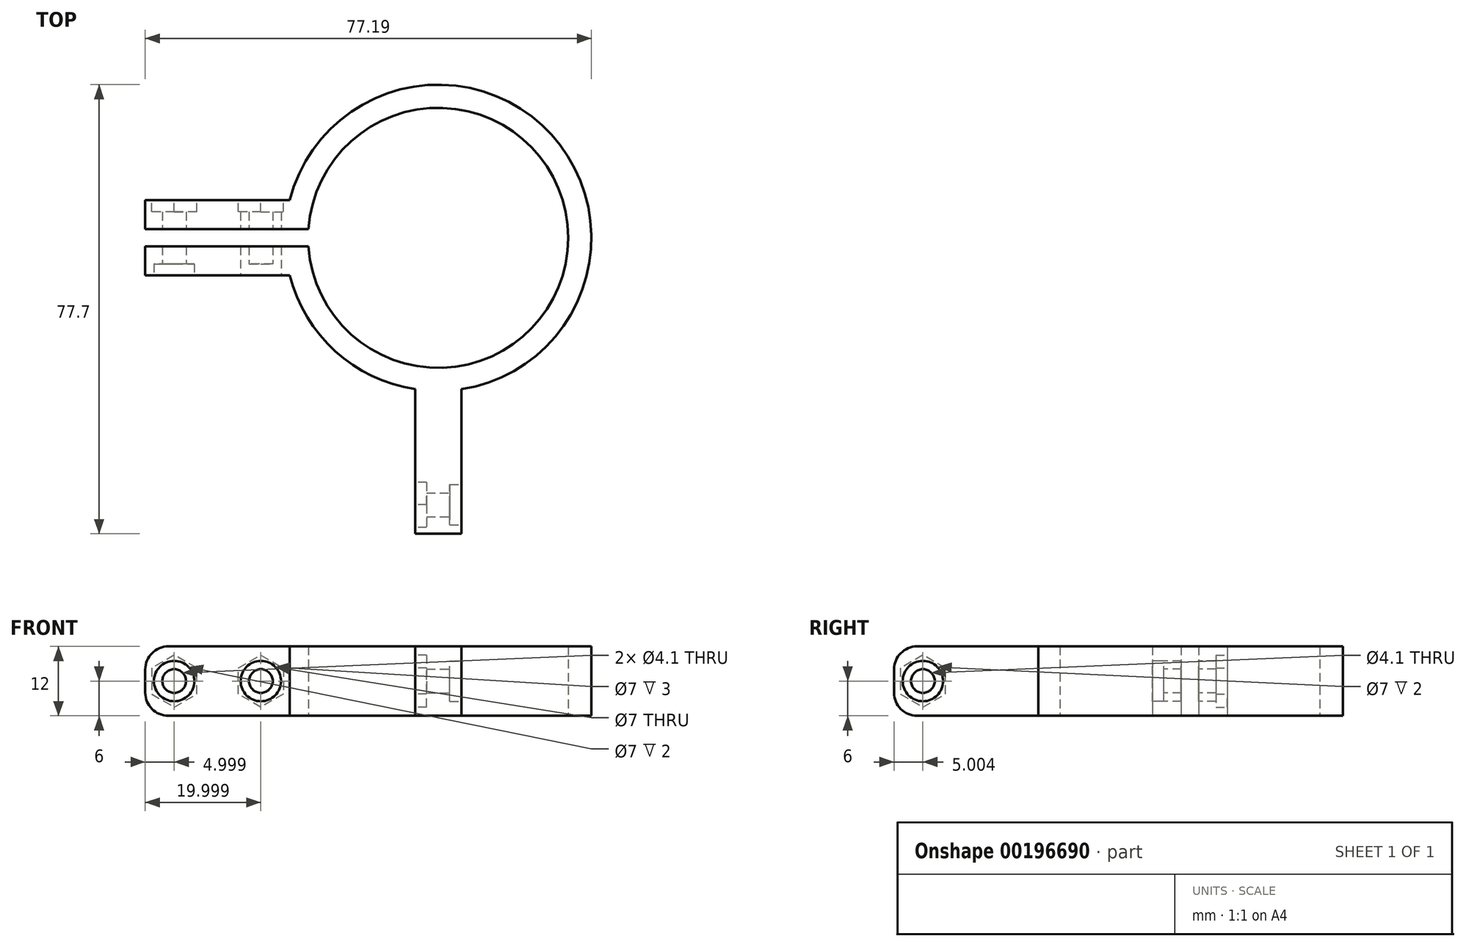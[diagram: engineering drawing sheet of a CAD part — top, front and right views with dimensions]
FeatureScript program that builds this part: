
annotation { "Feature Type Name" : "Feature", "Feature Type Description" : "" }
export const myFeature = defineFeature(function(context is Context, id is Id, definition is map)
    precondition{}
    {
        {
            var Q0;
            Q0=qCreatedBy(makeId("Top.planeOp"),FACE);
            var sketch = newSketch(context, id + "F0", { "sketchPlane" : qUnion([Q0])});
            skArc(sketch, "E0", {"start": v(-22.45, -1.5) * mm, "mid": v(22.5, 0) * mm, "end": v(-22.45, 1.5) * mm});
            skLineSegment(sketch, "E1.top", {"start": v(-25.7, -6.5) * mm, "end": v(-50.7, -6.5) * mm});
            skLineSegment(sketch, "E1.right", {"start": v(-50.7, 6.5) * mm, "end": v(-50.7, 1.5) * mm});
            skLineSegment(sketch, "E2", {"start": v(-22.45, 1.5) * mm, "end": v(-50.7, 1.5) * mm});
            skLineSegment(sketch, "E3", {"start": v(-22.45, -1.5) * mm, "end": v(-50.7, -1.5) * mm});
            skLineSegment(sketch, "E4.trimOffspring", {"start": v(-50.7, -1.5) * mm, "end": v(-50.7, -6.5) * mm});
            skLineSegment(sketch, "E5.trimOffspring", {"start": v(-25.7, 6.5) * mm, "end": v(-50.7, 6.5) * mm});
            skArc(sketch, "E6", {"start": v(-25.7, -6.5) * mm, "mid": v(-17.81, -19.62) * mm, "end": v(-4, -26.2) * mm});
            skLineSegment(sketch, "E7", {"start": v(0, 0) * mm, "end": v(-63.81, 0) * mm, "construction": true});
            skLineSegment(sketch, "E8", {"start": v(0, 0) * mm, "end": v(0, -56.86) * mm, "construction": true});
            skLineSegment(sketch, "E9.top", {"start": v(-4, -51.2) * mm, "end": v(4, -51.2) * mm});
            skLineSegment(sketch, "E9.left", {"start": v(-4, -26.2) * mm, "end": v(-4, -51.2) * mm});
            skLineSegment(sketch, "E9.right", {"start": v(4, -26.2) * mm, "end": v(4, -51.2) * mm});
            skArc(sketch, "E10.trimOffspring", {"start": v(4, -26.2) * mm, "mid": v(19.62, 17.81) * mm, "end": v(-25.7, 6.5) * mm});
            skSolve(sketch);
        }
        {
            var Q0;
            Q0=makeQuery(id+"F0.imprint","IMPRINT",FACE,{"disambiguationData":[TD([[makeQuery(id+"F0.imprint","IMPRINT",EDGE,{"derivedFrom":sQuery(id+"F0.wireOp",EDGE,"E0")}),-1.0]])]});
            extrude(context, id + "F1", {"entities" : qUnion([Q0]), "endBound" : BoundingType.SYMMETRIC, "depth" : 12 * mm});
        }
        {
            var Q0;
            Q0=makeQuery(id+"F1.opExtrude","SWEPT_FACE",FACE,{"disambiguationData":[OSD([sQuery(id+"F0.wireOp",EDGE,"E1.top")])]});
            var sketch = newSketch(context, id + "F2", { "sketchPlane" : qUnion([Q0])});
            skLineSegment(sketch, "E11", {"start": v(0, 0) * mm, "end": v(-145.87, 0) * mm, "construction": true});
            skPoint(sketch, "E12", {"position": v(-45.7, 0) * mm});
            skCircle(sketch, "E13", {"center": v(-45.7, 0) * mm, "radius": 2.05 * mm});
            skCircle(sketch, "E14", {"center": v(-45.7, 0) * mm, "radius": 3.5 * mm});
            skLineSegment(sketch, "E15", {"start": v(-38.2, 6) * mm, "end": v(-38.2, -6) * mm, "construction": true});
            skPoint(sketch, "E16.MirrorP", {"position": v(-30.7, 0) * mm});
            skCircle(sketch, "E17.MirrorC", {"center": v(-30.7, 0) * mm, "radius": 2.05 * mm});
            skCircle(sketch, "E18.MirrorC", {"center": v(-30.7, 0) * mm, "radius": 3.5 * mm});
            skSolve(sketch);
        }
        {
            var Q0;
            Q0=makeQuery(id+"F1.opExtrude","SWEPT_FACE",FACE,{"disambiguationData":[OSD([sQuery(id+"F0.wireOp",EDGE,"E5.trimOffspring")])]});
            var sketch = newSketch(context, id + "F3", { "sketchPlane" : qUnion([Q0])});
            skPoint(sketch, "E19", {"position": v(45.7, 0) * mm});
            skPoint(sketch, "E19.positionSnap0", {"position": v(50.7, 0) * mm});
            skCircle(sketch, "E20.cCircle", {"center": v(45.7, 0) * mm, "radius": 3.9 * mm, "construction": true});
            skLineSegment(sketch, "E20.0", {"start": v(49.59, 2.25) * mm, "end": v(49.59, -2.25) * mm});
            skLineSegment(sketch, "E20.1", {"start": v(49.59, -2.25) * mm, "end": v(45.7, -4.5) * mm});
            skLineSegment(sketch, "E20.2", {"start": v(45.7, -4.5) * mm, "end": v(41.8, -2.25) * mm});
            skLineSegment(sketch, "E20.3", {"start": v(41.8, -2.25) * mm, "end": v(41.8, 2.25) * mm});
            skLineSegment(sketch, "E20.4", {"start": v(41.8, 2.25) * mm, "end": v(45.7, 4.5) * mm});
            skLineSegment(sketch, "E20.5", {"start": v(45.7, 4.5) * mm, "end": v(49.59, 2.25) * mm});
            skPoint(sketch, "E20.0.midPoint", {"position": v(49.59, 0) * mm});
            skLineSegment(sketch, "E21", {"start": v(38.2, 6) * mm, "end": v(38.2, -6) * mm, "construction": true});
            skLineSegment(sketch, "E22.MirrorCS", {"start": v(30.7, 4.5) * mm, "end": v(26.8, 2.25) * mm});
            skLineSegment(sketch, "E23.MirrorCS", {"start": v(26.8, 2.25) * mm, "end": v(26.8, -2.25) * mm});
            skLineSegment(sketch, "E24.MirrorCS", {"start": v(30.7, -4.5) * mm, "end": v(34.59, -2.25) * mm});
            skLineSegment(sketch, "E25.MirrorCS", {"start": v(34.59, -2.25) * mm, "end": v(34.59, 2.25) * mm});
            skCircle(sketch, "E26.MirrorC", {"center": v(30.7, 0) * mm, "radius": 3.9 * mm, "construction": true});
            skPoint(sketch, "E27.MirrorP", {"position": v(26.8, 0) * mm});
            skLineSegment(sketch, "E28.MirrorCS", {"start": v(26.8, -2.25) * mm, "end": v(30.7, -4.5) * mm});
            skLineSegment(sketch, "E29.MirrorCS", {"start": v(34.59, 2.25) * mm, "end": v(30.7, 4.5) * mm});
            skSolve(sketch);
        }
        {
            var Q0;
            Q0=makeQuery(id+"F1.opExtrude","SWEPT_FACE",FACE,{"disambiguationData":[OSD([sQuery(id+"F0.wireOp",EDGE,"E9.right")])]});
            var sketch = newSketch(context, id + "F4", { "sketchPlane" : qUnion([Q0])});
            skLineSegment(sketch, "E30", {"start": v(0, 0) * mm, "end": v(-57.41, 0) * mm, "construction": true});
            skPoint(sketch, "E30.endSnap0", {"position": v(-51.2, 0) * mm});
            skPoint(sketch, "E31", {"position": v(-46.2, 0) * mm});
            skCircle(sketch, "E32", {"center": v(-46.2, 0) * mm, "radius": 2.05 * mm});
            skCircle(sketch, "E33", {"center": v(-46.2, 0) * mm, "radius": 3.5 * mm});
            skSolve(sketch);
        }
        {
            var Q0;
            Q0=makeQuery(id+"F1.opExtrude","SWEPT_FACE",FACE,{"disambiguationData":[OSD([sQuery(id+"F0.wireOp",EDGE,"E9.left")])]});
            var sketch = newSketch(context, id + "F5", { "sketchPlane" : qUnion([Q0])});
            skPoint(sketch, "E34", {"position": v(46.2, 0) * mm});
            skPoint(sketch, "E34.positionSnap0", {"position": v(51.2, 0) * mm});
            skCircle(sketch, "E35.cCircle", {"center": v(46.2, 0) * mm, "radius": 3.9 * mm, "construction": true});
            skLineSegment(sketch, "E35.0", {"start": v(50.1, 2.25) * mm, "end": v(50.1, -2.25) * mm});
            skLineSegment(sketch, "E35.1", {"start": v(50.1, -2.25) * mm, "end": v(46.2, -4.5) * mm});
            skLineSegment(sketch, "E35.2", {"start": v(46.2, -4.5) * mm, "end": v(42.3, -2.25) * mm});
            skLineSegment(sketch, "E35.3", {"start": v(42.3, -2.25) * mm, "end": v(42.3, 2.25) * mm});
            skLineSegment(sketch, "E35.4", {"start": v(42.3, 2.25) * mm, "end": v(46.2, 4.5) * mm});
            skLineSegment(sketch, "E35.5", {"start": v(46.2, 4.5) * mm, "end": v(50.1, 2.25) * mm});
            skPoint(sketch, "E35.0.midPoint", {"position": v(50.1, 0) * mm});
            skSolve(sketch);
        }
        {
            var Q0;
            Q0=makeQuery(id+"F5.imprint","IMPRINT",FACE,{"disambiguationData":[TD([[makeQuery(id+"F5.imprint","IMPRINT",EDGE,{"derivedFrom":sQuery(id+"F5.wireOp",EDGE,"E35.0")}),-1.0]])]});
            extrude(context, id + "F6", {"entities" : qUnion([Q0]), "operationType" : NewBodyOperationType.REMOVE, "oppositeDirection" : true, "depth" : 2 * mm});
        }
        {
            var Q0;
            Q0=makeQuery(id+"F3.imprint","IMPRINT",FACE,{"disambiguationData":[TD([[makeQuery(id+"F3.imprint","IMPRINT",EDGE,{"derivedFrom":sQuery(id+"F3.wireOp",EDGE,"E20.0")}),-1.0]])]});
            var Q1;
            Q1=makeQuery(id+"F3.imprint","IMPRINT",FACE,{"disambiguationData":[TD([[makeQuery(id+"F3.imprint","IMPRINT",EDGE,{"derivedFrom":sQuery(id+"F3.wireOp",EDGE,"E22.MirrorCS")}),1.0]])]});
            extrude(context, id + "F7", {"entities" : qUnion([Q0, Q1]), "operationType" : NewBodyOperationType.REMOVE, "oppositeDirection" : true, "depth" : 2 * mm});
        }
        {
            var Q0;
            Q0=makeQuery(id+"F2.imprint","IMPRINT",FACE,{"disambiguationData":[TD([[makeQuery(id+"F2.imprint","IMPRINT",EDGE,{"derivedFrom":sQuery(id+"F2.wireOp",EDGE,"E13")}),1.0]])]});
            var Q1;
            Q1=makeQuery(id+"F2.imprint","IMPRINT",FACE,{"disambiguationData":[TD([[makeQuery(id+"F2.imprint","IMPRINT",EDGE,{"derivedFrom":sQuery(id+"F2.wireOp",EDGE,"E17.MirrorC")}),-1.0]])]});
            var Q2;
            Q2=makeQuery(id+"F1.opExtrude","SWEPT_FACE",FACE,{"disambiguationData":[OSD([sQuery(id+"F0.wireOp",EDGE,"E5.trimOffspring")])]});
            extrude(context, id + "F8", {"entities" : qUnion([Q0, Q1]), "operationType" : NewBodyOperationType.REMOVE, "endBound" : BoundingType.UP_TO_SURFACE, "oppositeDirection" : true, "endBoundEntityFace" : qUnion([Q2]), "depth" : 25 * mm});
        }
        {
            var Q0;
            Q0=makeQuery(id+"F2.imprint","IMPRINT",FACE,{"disambiguationData":[TD([[makeQuery(id+"F2.imprint","IMPRINT",EDGE,{"derivedFrom":sQuery(id+"F2.wireOp",EDGE,"E13")}),-1.0]])]});
            var Q1;
            Q1=makeQuery(id+"F2.imprint","IMPRINT",FACE,{"disambiguationData":[TD([[makeQuery(id+"F2.imprint","IMPRINT",EDGE,{"derivedFrom":sQuery(id+"F2.wireOp",EDGE,"E17.MirrorC")}),1.0]])]});
            extrude(context, id + "F9", {"entities" : qUnion([Q0, Q1]), "operationType" : NewBodyOperationType.REMOVE, "oppositeDirection" : true, "depth" : 2 * mm});
        }
        {
            var Q0;
            Q0=makeQuery(id+"F4.imprint","IMPRINT",FACE,{"disambiguationData":[TD([[makeQuery(id+"F4.imprint","IMPRINT",EDGE,{"derivedFrom":sQuery(id+"F4.wireOp",EDGE,"E32")}),1.0]])]});
            var Q1;
            Q1=makeQuery(id+"F1.opExtrude","SWEPT_FACE",FACE,{"disambiguationData":[OSD([sQuery(id+"F0.wireOp",EDGE,"E9.left")])]});
            extrude(context, id + "F10", {"entities" : qUnion([Q0]), "operationType" : NewBodyOperationType.REMOVE, "endBound" : BoundingType.UP_TO_SURFACE, "oppositeDirection" : true, "endBoundEntityFace" : qUnion([Q1]), "depth" : 25 * mm});
        }
        {
            var Q0;
            Q0=makeQuery(id+"F4.imprint","IMPRINT",FACE,{"disambiguationData":[TD([[makeQuery(id+"F4.imprint","IMPRINT",EDGE,{"derivedFrom":sQuery(id+"F4.wireOp",EDGE,"E32")}),-1.0]])]});
            extrude(context, id + "F11", {"entities" : qUnion([Q0]), "operationType" : NewBodyOperationType.REMOVE, "oppositeDirection" : true, "depth" : 2 * mm});
        }
        {
            var Q0;
            Q0=makeQuery(id+"F1.opExtrude","CAP_EDGE",EDGE,{"disambiguationData":[OSD([sQuery(id+"F0.wireOp",EDGE,"E1.right")])],"isStart":false});
            var Q1;
            Q1=makeQuery(id+"F1.opExtrude","CAP_EDGE",EDGE,{"disambiguationData":[OSD([sQuery(id+"F0.wireOp",EDGE,"E1.right")])],"isStart":true});
            var Q2;
            Q2=makeQuery(id+"F1.opExtrude","CAP_EDGE",EDGE,{"disambiguationData":[OSD([sQuery(id+"F0.wireOp",EDGE,"E4.trimOffspring")])],"isStart":false});
            var Q3;
            Q3=makeQuery(id+"F1.opExtrude","CAP_EDGE",EDGE,{"disambiguationData":[OSD([sQuery(id+"F0.wireOp",EDGE,"E4.trimOffspring")])],"isStart":true});
            var Q4;
            Q4=makeQuery(id+"F1.opExtrude","CAP_EDGE",EDGE,{"disambiguationData":[OSD([sQuery(id+"F0.wireOp",EDGE,"E9.top")])],"isStart":false});
            var Q5;
            Q5=makeQuery(id+"F1.opExtrude","CAP_EDGE",EDGE,{"disambiguationData":[OSD([sQuery(id+"F0.wireOp",EDGE,"E9.top")])],"isStart":true});
            fillet(context, id + "F12", {"entities" : qUnion([Q0, Q1, Q2, Q3, Q4, Q5]), "radius" : 4 * mm, "tangentPropagation" : true, "allowEdgeOverflow" : false});
        }
    });
